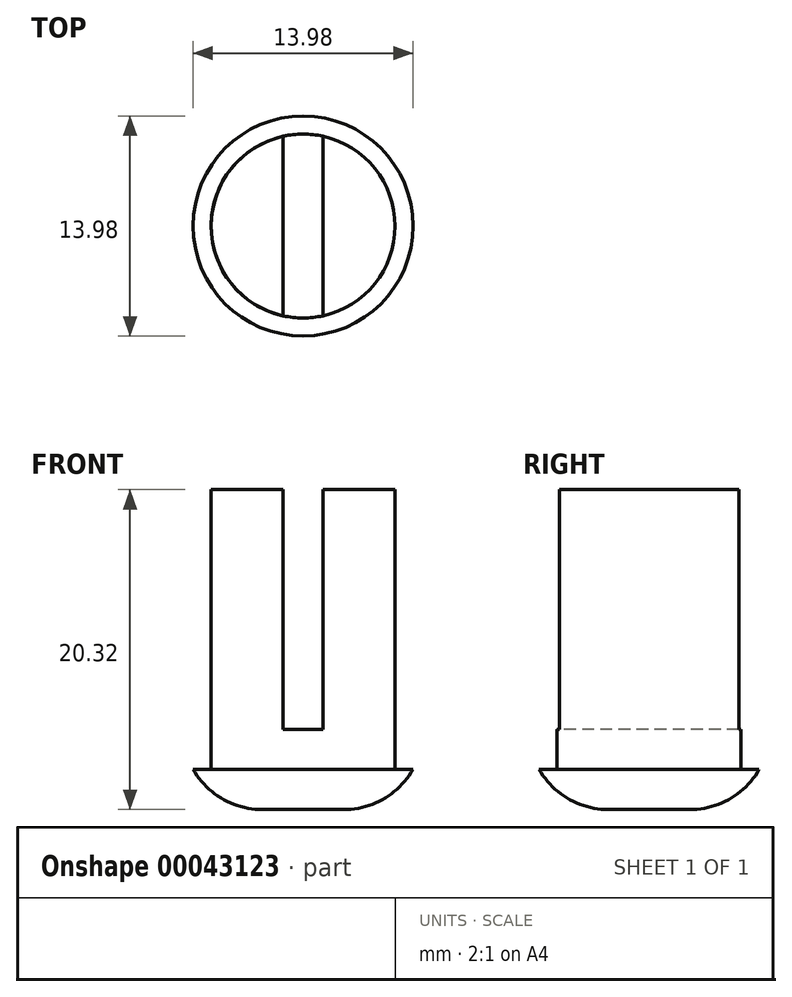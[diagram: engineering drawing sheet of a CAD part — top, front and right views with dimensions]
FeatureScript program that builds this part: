
annotation { "Feature Type Name" : "Feature", "Feature Type Description" : "" }
export const myFeature = defineFeature(function(context is Context, id is Id, definition is map)
    precondition{}
    {
        {
            var Q0;
            Q0=qCreatedBy(makeId("Top.planeOp"),FACE);
            var sketch = newSketch(context, id + "F0", { "sketchPlane" : qUnion([Q0])});
            skCircle(sketch, "E0", {"center": v(0, 0) * mm, "radius": 5.84 * mm});
            skSolve(sketch);
        }
        {
            var Q0;
            Q0=makeQuery(id+"F0.imprint","IMPRINT",FACE,{"disambiguationData":[TD([[makeQuery(id+"F0.imprint","IMPRINT",EDGE,{"derivedFrom":sQuery(id+"F0.wireOp",EDGE,"E0")}),1.0]])]});
            extrude(context, id + "F1", {"entities" : qUnion([Q0]), "depth" : 17.78 * mm});
        }
        {
            var Q0;
            Q0=makeQuery(id+"F1.opExtrude","CAP_FACE",FACE,{"disambiguationData":[OSD([sQuery(id+"F0.wireOp",EDGE,"E0")])],"isStart":false});
            var sketch = newSketch(context, id + "F2", { "sketchPlane" : qUnion([Q0])});
            skLineSegment(sketch, "E1.rect.bottom", {"start": v(1.27, 11.24) * mm, "end": v(-1.27, 11.24) * mm});
            skLineSegment(sketch, "E1.rect.top", {"start": v(1.27, -11.24) * mm, "end": v(-1.27, -11.24) * mm});
            skLineSegment(sketch, "E1.rect.left", {"start": v(1.27, 11.24) * mm, "end": v(1.27, -11.24) * mm});
            skLineSegment(sketch, "E1.rect.right", {"start": v(-1.27, 11.24) * mm, "end": v(-1.27, -11.24) * mm});
            skPoint(sketch, "E1.rect.middle", {"position": v(0, 0) * mm});
            skSolve(sketch);
        }
        {
            var Q0;
            {var subQ1=makeQuery(id+"F1.opExtrude","CAP_EDGE",EDGE,{"disambiguationData":[OSD([sQuery(id+"F0.wireOp",EDGE,"E0")])],"isStart":false});var subQ4=sQuery(id+"F2.wireOp",EDGE,"E1.rect.left");var subQ6=makeQuery(id+"F2.imprint","INTERSECT",VERTEX,{"disambiguationData":[OD(0.0)],"derivedFrom":[subQ1,subQ4]});Q0=makeQuery(id+"F2.imprint","IMPRINT",FACE,{"disambiguationData":[TD([[makeQuery(id+"F2.imprint","IMPRINT",EDGE,{"disambiguationData":[TD([[subQ6,-1.0]])],"derivedFrom":subQ4}),-1.0]])]});}
            extrude(context, id + "F3", {"entities" : qUnion([Q0]), "operationType" : NewBodyOperationType.REMOVE, "oppositeDirection" : true, "depth" : 15.24 * mm});
        }
        {
            var Q0;
            Q0=makeQuery(id+"F1.opExtrude","CAP_FACE",FACE,{"disambiguationData":[OSD([sQuery(id+"F0.wireOp",EDGE,"E0")])],"isStart":true});
            var sketch = newSketch(context, id + "F4", { "sketchPlane" : qUnion([Q0])});
            skCircle(sketch, "E2", {"center": v(0, 0) * mm, "radius": 6.99 * mm});
            skSolve(sketch);
        }
        {
            var Q0;
            Q0=makeQuery(id+"F4.imprint","IMPRINT",FACE,{"disambiguationData":[TD([[makeQuery(id+"F4.imprint","IMPRINT",EDGE,{"derivedFrom":sQuery(id+"F4.wireOp",EDGE,"E2")}),1.0]])]});
            var Q1;
            Q1=makeQuery(id+"F4.imprint","IMPRINT",FACE,{"disambiguationData":[TD([[makeQuery(id+"F4.imprint","IMPRINT",EDGE,{"derivedFrom":makeQuery(id+"F1.opExtrude","CAP_EDGE",EDGE,{"disambiguationData":[OSD([sQuery(id+"F0.wireOp",EDGE,"E0")])],"isStart":true})}),-1.0]])]});
            extrude(context, id + "F5", {"entities" : qUnion([Q0, Q1]), "operationType" : NewBodyOperationType.ADD, "depth" : 2.54 * mm});
        }
        {
            var Q0;
            Q0=makeQuery(id+"F5.opExtrude","CAP_FACE",FACE,{"disambiguationData":[OSD([sQuery(id+"F4.wireOp",EDGE,"E2")])],"isStart":false});
            fillet(context, id + "F6", {"entities" : qUnion([Q0]), "radius" : 5.08 * mm, "tangentPropagation" : true, "allowEdgeOverflow" : false});
        }
    });
